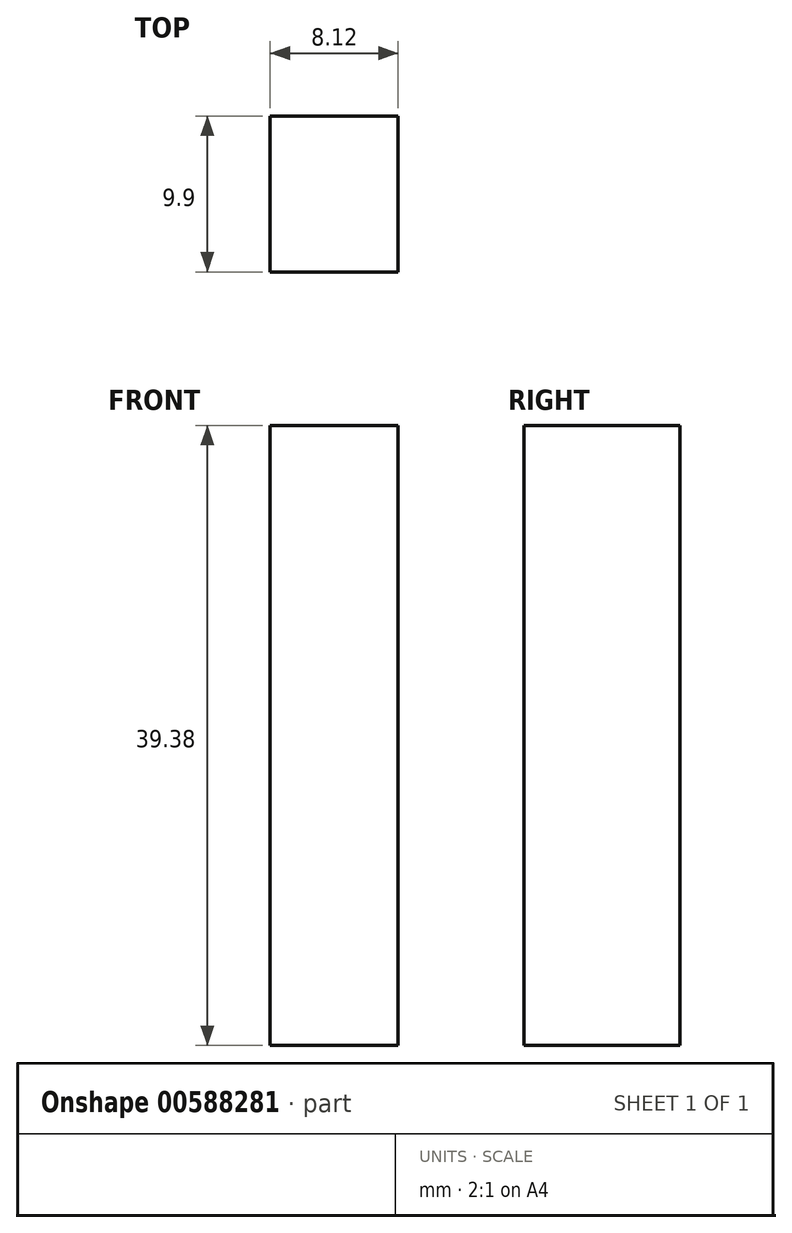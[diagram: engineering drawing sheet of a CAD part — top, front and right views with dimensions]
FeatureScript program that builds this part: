
annotation { "Feature Type Name" : "Feature", "Feature Type Description" : "" }
export const myFeature = defineFeature(function(context is Context, id is Id, definition is map)
    precondition{}
    {
        {
            var Q0;
            Q0=qCreatedBy(makeId("Front.planeOp"),FACE);
            var sketch = newSketch(context, id + "F0", { "sketchPlane" : qUnion([Q0])});
            skLineSegment(sketch, "E0.bottom", {"start": v(37.85, 19.69) * mm, "end": v(-37.85, 19.69) * mm});
            skLineSegment(sketch, "E0.top", {"start": v(37.85, -19.69) * mm, "end": v(-37.85, -19.69) * mm});
            skLineSegment(sketch, "E0.left", {"start": v(37.85, 19.69) * mm, "end": v(37.85, -19.68) * mm});
            skLineSegment(sketch, "E0.right", {"start": v(-37.85, 19.69) * mm, "end": v(-37.85, -19.69) * mm});
            skPoint(sketch, "E0.middle", {"position": v(0, 0) * mm});
            skSolve(sketch);
        }
        {
            var Q0;
            Q0=makeQuery(id+"F0.imprint","IMPRINT",FACE,{"disambiguationData":[TD([[makeQuery(id+"F0.imprint","IMPRINT",EDGE,{"derivedFrom":sQuery(id+"F0.wireOp",EDGE,"E0.bottom")}),1.0]])]});
            extrude(context, id + "F1", {"entities" : qUnion([Q0]), "endBound" : BoundingType.SYMMETRIC, "depth" : 9.9 * mm, "offsetDistance" : 25.4 * mm});
        }
        {
            var Q0;
            Q0=makeQuery(id+"F1.opExtrude","SWEPT_FACE",FACE,{"disambiguationData":[OSD([sQuery(id+"F0.wireOp",EDGE,"E0.bottom")])]});
            var sketch = newSketch(context, id + "F2", { "sketchPlane" : qUnion([Q0])});
            skLineSegment(sketch, "E1.right", {"start": v(-4.06, 6.48) * mm, "end": v(-4.06, -4.95) * mm});
            skLineSegment(sketch, "E2.bottom", {"start": v(-4.06, 6.48) * mm, "end": v(0, 6.48) * mm});
            skLineSegment(sketch, "E2.top", {"start": v(-4.06, -4.95) * mm, "end": v(0, -4.95) * mm});
            skLineSegment(sketch, "E2.right", {"start": v(0, 6.48) * mm, "end": v(0, -4.95) * mm});
            skLineSegment(sketch, "E3.MirrorCS", {"start": v(4.06, 6.48) * mm, "end": v(4.06, -4.95) * mm});
            skLineSegment(sketch, "E4.MirrorCS", {"start": v(4.06, -4.95) * mm, "end": v(0, -4.95) * mm});
            skLineSegment(sketch, "E5.MirrorCS", {"start": v(4.06, 6.48) * mm, "end": v(0, 6.48) * mm});
            skLineSegment(sketch, "E6.bottom", {"start": v(-4.06, 6.48) * mm, "end": v(-37.85, 6.48) * mm});
            skLineSegment(sketch, "E6.top", {"start": v(-4.06, -4.95) * mm, "end": v(-37.85, -4.95) * mm});
            skLineSegment(sketch, "E6.right", {"start": v(-37.85, 6.48) * mm, "end": v(-37.85, -4.95) * mm});
            skLineSegment(sketch, "E7.bottom", {"start": v(4.06, 6.48) * mm, "end": v(37.85, 6.48) * mm});
            skLineSegment(sketch, "E7.top", {"start": v(4.06, -4.95) * mm, "end": v(37.85, -4.95) * mm});
            skLineSegment(sketch, "E7.right", {"start": v(37.85, 6.48) * mm, "end": v(37.85, -4.95) * mm});
            skLineSegment(sketch, "E8.bottom", {"start": v(-4.06, 6.48) * mm, "end": v(-39.4, 6.48) * mm});
            skLineSegment(sketch, "E8.top", {"start": v(-4.06, -19.75) * mm, "end": v(-39.4, -19.75) * mm});
            skLineSegment(sketch, "E8.left", {"start": v(-4.06, 6.48) * mm, "end": v(-4.06, -19.75) * mm});
            skLineSegment(sketch, "E8.right", {"start": v(-39.4, 6.48) * mm, "end": v(-39.4, -19.75) * mm});
            skLineSegment(sketch, "E9.bottom", {"start": v(4.06, 6.48) * mm, "end": v(39.7, 6.48) * mm});
            skLineSegment(sketch, "E9.top", {"start": v(4.06, -21.63) * mm, "end": v(39.7, -21.63) * mm});
            skLineSegment(sketch, "E9.left", {"start": v(4.06, 6.48) * mm, "end": v(4.06, -21.63) * mm});
            skLineSegment(sketch, "E9.right", {"start": v(39.7, 6.48) * mm, "end": v(39.7, -21.63) * mm});
            skSolve(sketch);
        }
        {
            var Q0;
            {var subQ5=sQuery(id+"F2.wireOp",EDGE,"E6.top");Q0=makeQuery(id+"F2.imprint","IMPRINT",FACE,{"disambiguationData":[TD([[makeQuery(id+"F2.imprint","IMPRINT",EDGE,{"derivedFrom":subQ5}),1.0]])]});}
            var Q1;
            {var subQ2=sQuery(id+"F2.wireOp",EDGE,"E7.top");Q1=makeQuery(id+"F2.imprint","IMPRINT",FACE,{"disambiguationData":[TD([[makeQuery(id+"F2.imprint","IMPRINT",EDGE,{"derivedFrom":subQ2}),1.0]])]});}
            var Q2;
            {var subQ0=sQuery(id+"F2.wireOp",EDGE,"E7.top");Q2=makeQuery(id+"F2.imprint","IMPRINT",FACE,{"disambiguationData":[TD([[makeQuery(id+"F2.imprint","IMPRINT",EDGE,{"derivedFrom":subQ0}),-1.0]])]});}
            var Q3;
            {var subQ0=sQuery(id+"F2.wireOp",EDGE,"E6.top");Q3=makeQuery(id+"F2.imprint","IMPRINT",FACE,{"disambiguationData":[TD([[makeQuery(id+"F2.imprint","IMPRINT",EDGE,{"derivedFrom":subQ0}),-1.0]])]});}
            var Q4;
            {var subQ0=sQuery(id+"F2.wireOp",EDGE,"E6.right");var subQ3=sQuery(id+"F2.wireOp",EDGE,"E8.bottom");var subQ4=makeQuery(id+"F2.imprint","INTERSECT",VERTEX,{"derivedFrom":[subQ0,subQ3]});Q4=makeQuery(id+"F2.imprint","IMPRINT",FACE,{"disambiguationData":[TD([[makeQuery(id+"F2.imprint","IMPRINT",EDGE,{"disambiguationData":[TD([[subQ4,-1.0]])],"derivedFrom":subQ0}),1.0]])]});}
            var Q5;
            {var subQ0=sQuery(id+"F2.wireOp",EDGE,"E7.right");var subQ3=sQuery(id+"F2.wireOp",EDGE,"E9.bottom");var subQ4=makeQuery(id+"F2.imprint","INTERSECT",VERTEX,{"derivedFrom":[subQ0,subQ3]});Q5=makeQuery(id+"F2.imprint","IMPRINT",FACE,{"disambiguationData":[TD([[makeQuery(id+"F2.imprint","IMPRINT",EDGE,{"disambiguationData":[TD([[subQ4,-1.0]])],"derivedFrom":subQ0}),-1.0]])]});}
            var Q6;
            {var subQ0=sQuery(id+"F2.wireOp",EDGE,"E5.MirrorCS");Q6=makeQuery(id+"F2.imprint","IMPRINT",FACE,{"disambiguationData":[TD([[makeQuery(id+"F2.imprint","IMPRINT",EDGE,{"derivedFrom":subQ0}),1.0]])]});}
            var Q7;
            {var subQ0=sQuery(id+"F2.wireOp",EDGE,"E2.bottom");Q7=makeQuery(id+"F2.imprint","IMPRINT",FACE,{"disambiguationData":[TD([[makeQuery(id+"F2.imprint","IMPRINT",EDGE,{"derivedFrom":subQ0}),-1.0]])]});}
            extrude(context, id + "F3", {"entities" : qUnion([Q0, Q1, Q2, Q3, Q4, Q5, Q6, Q7]), "operationType" : NewBodyOperationType.REMOVE, "oppositeDirection" : true, "depth" : 76.2 * mm, "offsetDistance" : 25.4 * mm});
        }
    });
